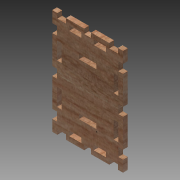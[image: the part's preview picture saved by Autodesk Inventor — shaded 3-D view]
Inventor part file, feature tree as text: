
AUTODESK INVENTOR PART (.ipt)
format: ipt  version: 2015 (Build 190159000, 159)  size: 408,064 bytes
history: native  units: mm
features: other x7, extrude x6, sketch x6
ambient origin geometry x8: Origin, YZ Plane, XZ Plane, XY Plane, X Axis, Y Axis, Z Axis, Center Point
bodies: Solid1 (feature_tree)
feature tree (19):
  other  "Blocks"
  extrude  "Extrusion1"  Depth=111.0mm
  extrude  "Extrusion2"  Depth=40.0mm
  extrude  "Extrusion13"  Depth=5.5mm
  extrude  "Extrusion15"  Depth=22.166667mm
  extrude  "Extrusion17"  Depth=14.2mm
  extrude  "Extrusion18"  Depth=10.0mm TaperAngle=0.0deg
  sketch  "Sketch1"  dims[d0=71.0mm d1=111.0mm]
  sketch  "Sketch6"  dims[d2=5.5mm d3=0.0mm d22=40.0mm]
  other  "Block1"
  other  "Block2"
  other  "Block3"
  other  "Block4"
  other  "Block5"
  other  "Block6"
  sketch  "Sketch26"  dims[d23=80.0mm d38=5.5mm]
  sketch  "Sketch27"  dims[d39=5.5mm d40=22.166667mm]
  sketch  "Sketch28"  dims[d41=20.0mm d42=14.2mm]
  sketch  "Sketch29"  dims[d43=14.2mm d44=10.0mm d45=0.0mm d59=11.0mm d60=5.0mm d62=11.0mm d63=5.0mm d126=5.5mm d127=5.5mm d128=5.5mm d129=0.0mm d132=5.0mm d133=10.0mm d137=5.5mm d138=0.0mm d139=4.0mm d140=5.5mm d141=10.0mm d142=5.5mm d146=5.5mm d147=0.0mm d148=25.0mm d149=38.0mm d150=20.0mm d151=5.5mm d152=60.0mm d153=5.5mm d154=0.0mm d26=1.0mm d27=1.0mm]
